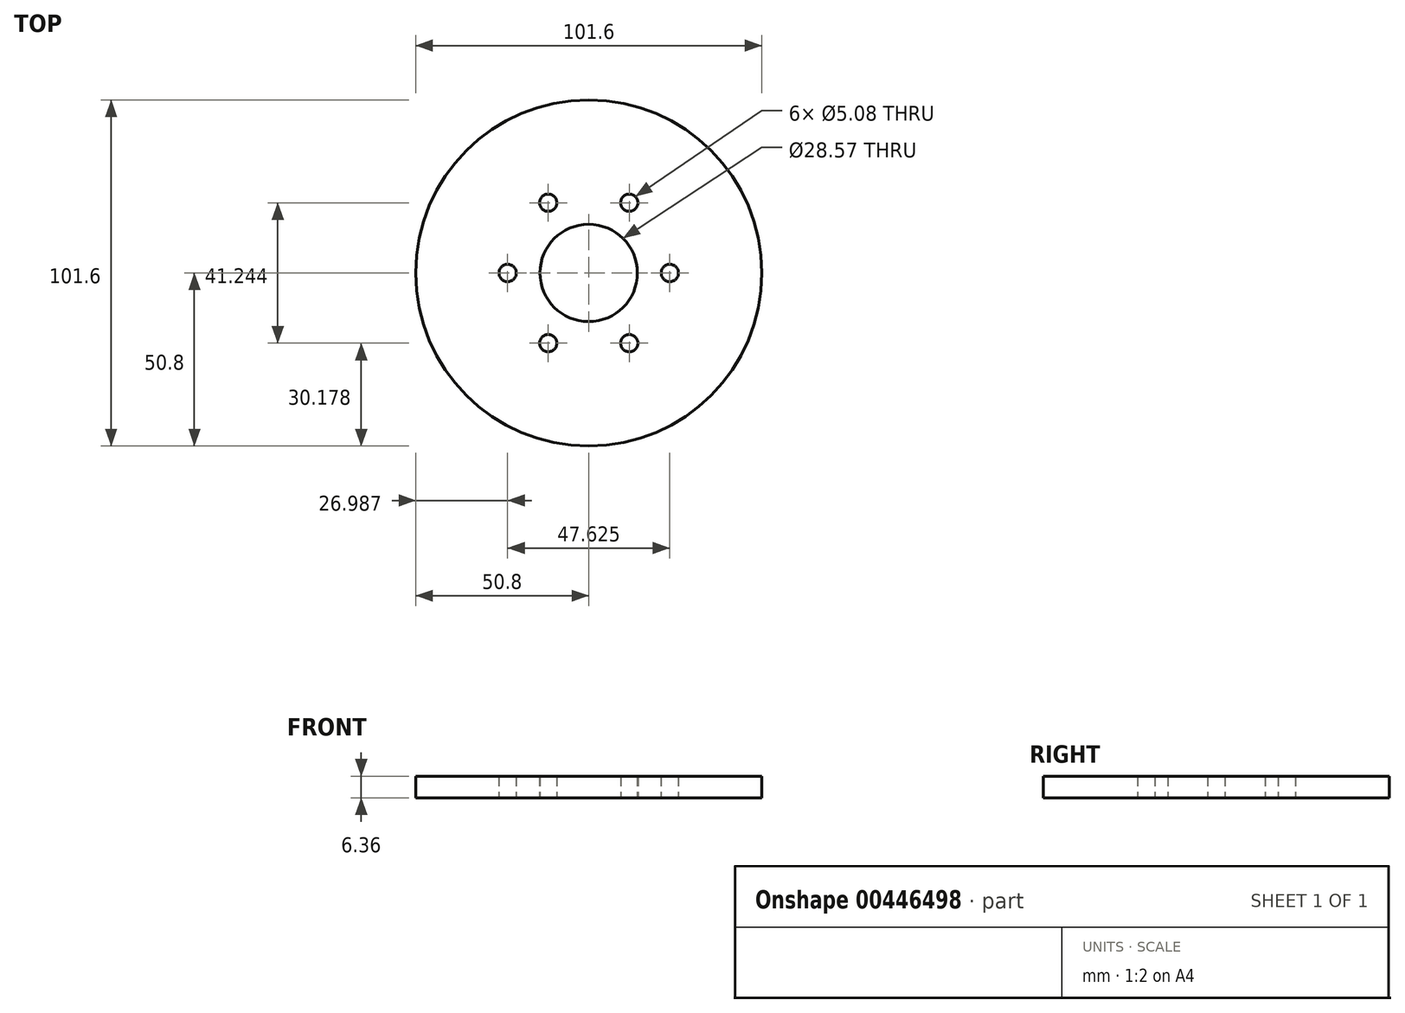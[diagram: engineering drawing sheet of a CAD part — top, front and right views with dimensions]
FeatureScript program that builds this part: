
annotation { "Feature Type Name" : "Feature", "Feature Type Description" : "" }
export const myFeature = defineFeature(function(context is Context, id is Id, definition is map)
    precondition{}
    {
        {
            var Q0;
            Q0=qCreatedBy(makeId("Top.planeOp"),FACE);
            var sketch = newSketch(context, id + "F0", { "sketchPlane" : qUnion([Q0])});
            skCircle(sketch, "E0", {"center": v(0, 0) * mm, "radius": 50.8 * mm});
            skCircle(sketch, "E1", {"center": v(0, 0) * mm, "radius": 23.81 * mm, "construction": true});
            skCircle(sketch, "E2", {"center": v(23.81, 0) * mm, "radius": 2.54 * mm});
            skCircle(sketch, "E3.1.0", {"center": v(11.9, -20.62) * mm, "radius": 2.54 * mm});
            skCircle(sketch, "E3.2.0", {"center": v(-11.9, -20.62) * mm, "radius": 2.54 * mm});
            skCircle(sketch, "E3.3.0", {"center": v(-23.81, 0) * mm, "radius": 2.54 * mm});
            skCircle(sketch, "E3.4.0", {"center": v(-11.9, 20.62) * mm, "radius": 2.54 * mm});
            skCircle(sketch, "E3.5.0", {"center": v(11.9, 20.62) * mm, "radius": 2.54 * mm});
            skLineSegment(sketch, "E3.anchor1", {"start": v(0, 0) * mm, "end": v(23.81, 0) * mm, "construction": true});
            skLineSegment(sketch, "E3.anchor2", {"start": v(0, 0) * mm, "end": v(11.9, 20.62) * mm, "construction": true});
            skCircle(sketch, "E4", {"center": v(0, 0) * mm, "radius": 14.29 * mm});
            skSolve(sketch);
        }
        {
            var Q0;
            Q0=makeQuery(id+"F0.imprint","IMPRINT",FACE,{"disambiguationData":[TD([[makeQuery(id+"F0.imprint","IMPRINT",EDGE,{"derivedFrom":sQuery(id+"F0.wireOp",EDGE,"E0")}),1.0]])]});
            extrude(context, id + "F1", {"entities" : qUnion([Q0]), "depth" : 6.35 * mm, "symmetric" : true});
        }
    });
